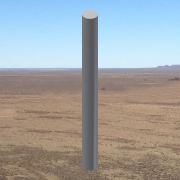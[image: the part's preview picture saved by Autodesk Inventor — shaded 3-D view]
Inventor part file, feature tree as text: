
AUTODESK INVENTOR PART (.ipt)
format: ipt  version: 2013 SP2 (Build 170200200, 200)  size: 137,728 bytes
history: native  units: in
note: dims shown in document units (in); Inventor stores cm internally (conversion verified against a paired STEP export)
features: extrude x1, sketch x1
ambient origin geometry x8: Origin, YZ Plane, XZ Plane, XY Plane, X Axis, Y Axis, Z Axis, Center Point
bodies: Solid1 (feature_tree)
feature tree (2):
  extrude  "Extrusion1"  Depth=5.75in TaperAngle=0.0deg
  sketch  "Sketch1"  dims[d0=0.5in d1=5.75in d2=0.0in]
